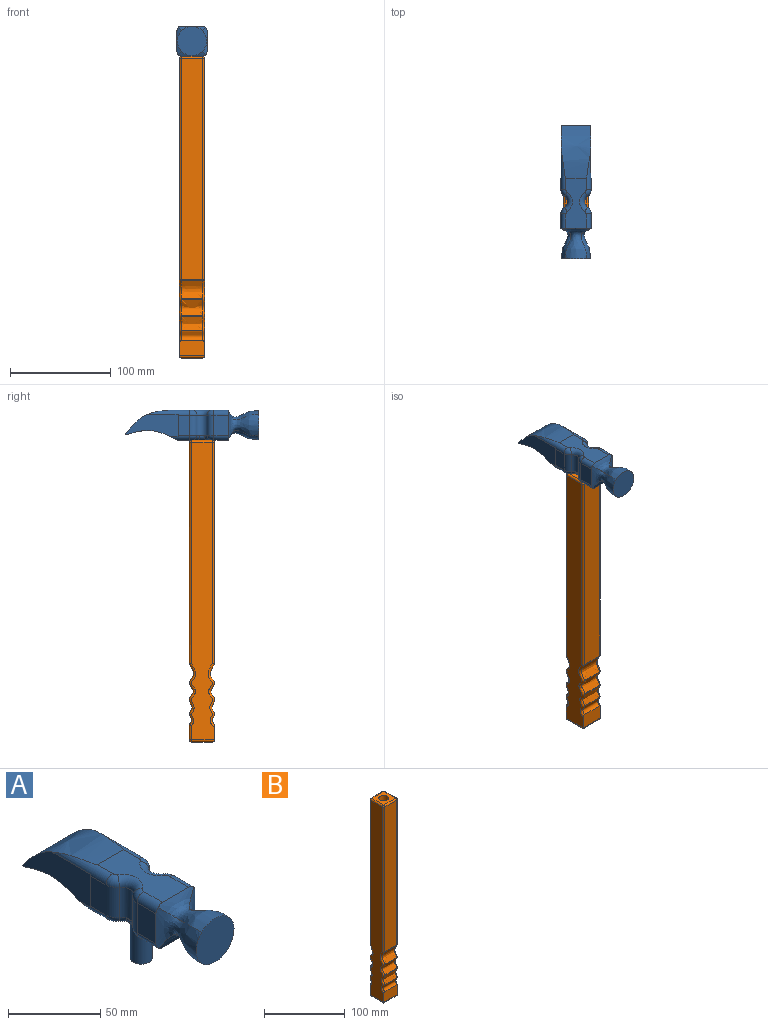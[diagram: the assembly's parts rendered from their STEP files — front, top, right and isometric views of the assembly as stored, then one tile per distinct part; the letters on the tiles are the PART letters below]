
ASSEMBLY  parts=2 mates=1
PART A: 51 faces, bbox 30x133.1x55 mm
  f0: plane 22.18x20mm, normal (0,0,-1), area 388.1mm2, adj f9,f25,f36,f37,f38,f43,f44,f45
  f1: plane 50x20mm, normal (0,0,1), area 812.3mm2, adj f11,f16,f27,f28,f29,f30,f31,f46
  f2: plane 20x11.8mm, normal (1,0,0), area 235.9mm2, adj f6,f21,f27,f32
  f3: plane 20x19.63mm, normal (0,0,-1), area 337.1mm2, adj f14,f25,f32,f33,f34,f39,f40,f41
  f4: plane 20x14.35mm, normal (-1,0,0), area 286.9mm2, adj f8,f23,f45,f50
  f5: plane 20x11.8mm, normal (-1,0,0), area 235.9mm2, adj f13,f24,f39,f46
  f6: plane 21.99x0.1mm, normal (0,1,0), area 2.1mm2, adj f2,f17,f27,f32
  f7: plane 29.01x29.01mm, normal (0,-1,0), area 660.9mm2, adj f8,f9,f10,f11
  f8: bspline ~30.4x30mm, area 683.9mm2, adj f4,f7,f9,f11,f45,f50
  f9: bspline ~30.4x30mm, area 683.9mm2, adj f0,f7,f8,f10,f38,f45
  f10: bspline ~30.4x30mm, area 683.9mm2, adj f7,f9,f11,f12,f31,f38
  f11: bspline ~30.4x30mm, area 683.9mm2, adj f1,f7,f8,f10,f31,f50
  f12: plane 20x14.35mm, normal (1,0,0), area 286.9mm2, adj f10,f22,f31,f38
  f13: plane 21.99x0.1mm, normal (0,1,0), area 2.1mm2, adj f5,f18,f39,f46
  f14: extruded ~51.69x29.8mm, area 1587.3mm2, adj f3,f15,f17,f18,f32,f39
  f15: plane 29.8x1.02mm, normal (0,0.32,-0.95), area 31.9mm2, adj f14,f16,f17,f18
  f16: extruded ~52.71x29.8mm, area 1671.4mm2, adj f1,f15,f17,f18,f27,f46
  f17: plane 52.71x22.75mm, normal (1,0,0), area 797.5mm2, adj f6,f14,f15,f16,f27,f32
  f18: plane 52.71x22.75mm, normal (-1,0,0), area 797.5mm2, adj f13,f14,f15,f16,f39,f46
  f19: cylinder r=6.36mm len=20mm, axis (0,0,1), area 249.4mm2, adj f23,f24,f41,f42,f43,f48
  f20: cylinder r=6.36mm len=20mm, axis (0,0,1), area 249.4mm2, adj f21,f22,f29,f34,f35,f36
  f21: cylinder r=8mm len=20mm, axis (0,0,1), area 156.8mm2, adj f2,f20,f28,f33
  f22: cylinder r=8mm len=20mm, axis (0,0,1), area 156.8mm2, adj f12,f20,f30,f37
  f23: cylinder r=8mm len=20mm, axis (0,0,1), area 156.8mm2, adj f4,f19,f44,f49
  f24: cylinder r=8mm len=20mm, axis (0,0,1), area 156.8mm2, adj f5,f19,f40,f47
  f25: cylinder r=6.01mm len=25mm, axis (0,0,1), area 944.8mm2, adj f0,f3,f26,f35,f42
  f26: plane 12.03x12.03mm, normal (0,0,-1), area 113.6mm2, adj f25
  f27: cylinder r=5mm len=41.57mm, axis (0,-1,0), area 204.3mm2, adj f1,f2,f6,f16,f17,f28
  f28: torus R=3mm, axis (0,0,1), area 47.6mm2, adj f1,f21,f27,f29
  f29: torus R=11.36mm, axis (0,0,1), area 125.9mm2, adj f1,f20,f28,f30
  f30: torus R=3mm, axis (0,0,1), area 47.6mm2, adj f1,f22,f29,f31
  f31: cylinder r=5mm len=14.92mm, axis (0,-1,0), area 114.9mm2, adj f1,f10,f11,f12,f30
  f32: cylinder r=5mm len=20.37mm, axis (0,-1,0), area 113.3mm2, adj f2,f3,f6,f14,f17,f33
  f33: torus R=3mm, axis (0,0,-1), area 47.6mm2, adj f3,f21,f32,f34
  f34: torus R=11.36mm, axis (0,0,-1), area 39.3mm2, adj f3,f20,f33,f35
  f35: bspline ~8.2x5mm, area 34.4mm2, adj f20,f25,f34,f36
  f36: torus R=11.36mm, axis (0,0,-1), area 39.3mm2, adj f0,f20,f35,f37
  f37: torus R=3mm, axis (0,0,-1), area 47.6mm2, adj f0,f22,f36,f38
  f38: cylinder r=5mm len=14.92mm, axis (0,-1,0), area 114.9mm2, adj f0,f9,f10,f12,f37
  f39: cylinder r=5mm len=20.37mm, axis (0,-1,0), area 113.3mm2, adj f3,f5,f13,f14,f18,f40
  f40: torus R=3mm, axis (0,0,-1), area 47.6mm2, adj f3,f24,f39,f41
  f41: torus R=11.36mm, axis (0,0,-1), area 39.3mm2, adj f3,f19,f40,f42
  f42: bspline ~8.2x5mm, area 34.4mm2, adj f19,f25,f41,f43
  f43: torus R=11.36mm, axis (0,0,-1), area 39.3mm2, adj f0,f19,f42,f44
  f44: torus R=3mm, axis (0,0,-1), area 47.6mm2, adj f0,f23,f43,f45
  f45: cylinder r=5mm len=14.92mm, axis (0,-1,0), area 114.9mm2, adj f0,f4,f8,f9,f44
  f46: cylinder r=5mm len=41.57mm, axis (0,-1,0), area 204.3mm2, adj f1,f5,f13,f16,f18,f47
  f47: torus R=3mm, axis (0,0,1), area 47.6mm2, adj f1,f24,f46,f48
  f48: torus R=11.36mm, axis (0,0,1), area 125.9mm2, adj f1,f19,f47,f49
  f49: torus R=3mm, axis (0,0,1), area 47.6mm2, adj f1,f23,f48,f50
  f50: cylinder r=5mm len=14.92mm, axis (0,-1,0), area 114.9mm2, adj f1,f4,f8,f11,f49
PART B: 51 faces, bbox 25.2x30.6x300.2 mm
  f0: plane 23.32x0.47mm, normal (0,1,0), area 6mm2, adj f9,f16,f23,f42
  f1: plane 23.33x0.91mm, normal (0,1,0), area 21.2mm2, adj f9,f22,f23,f42
  f2: plane 23x0.2mm, normal (0,1,0), area 4.5mm2, adj f9,f21,f22,f45
  f3: plane 220.5x21mm, normal (0,1,0), area 4630.6mm2, adj f16,f30,f36,f39
  f4: plane 296x22.89mm, normal (-1,0,0), area 5923mm2, adj f11,f29,f33,f37,f39,f42,f45,f46
  f5: plane 21.33x0.36mm, normal (0,-1,0), area 4.1mm2, adj f19,f20,f24,f29
  f6: plane 21.65x0.91mm, normal (0,-1,0), area 19.6mm2, adj f18,f19,f24,f29
  f7: plane 21.42x0.47mm, normal (0,-1,0), area 5.5mm2, adj f17,f18,f24,f29
  f8: plane 219.94x21mm, normal (0,-1,0), area 4618.7mm2, adj f25,f28,f32,f33
  f9: plane 296x25.18mm, normal (1,0,0), area 6096.6mm2, adj f0,f1,f2,f11,f16,f21,f22,f23
  f10: plane 21x15.32mm, normal (0,1,0), area 321.7mm2, adj f21,f41,f47,f50
  f11: plane 25x15.32mm, normal (0,-1,0), area 380.4mm2, adj f4,f9,f20,f24,f29,f43
  f12: plane 21x20.85mm, normal (0,0,1), area 324.3mm2, adj f14,f31,f32,f36,f37
  f13: plane 21x20.85mm, normal (0,0,-1), area 437.9mm2, adj f40,f43,f46,f47
  f14: cylinder r=6.02mm len=24.8mm, axis (0,0,1), area 937.3mm2, adj f12,f15
  f15: plane 12.03x12.03mm, normal (0,0,1), area 113.7mm2, adj f14
  f16: extruded ~23x18.71mm, area 475.5mm2, adj f0,f3,f9,f30,f42
  f17: extruded ~21x18.23mm, area 425.8mm2, adj f7,f24,f28,f29
  f18: extruded ~21x15.96mm, area 377.8mm2, adj f6,f7,f24,f29
  f19: extruded ~21x13.87mm, area 313.7mm2, adj f5,f6,f24,f29
  f20: extruded ~21x10.27mm, area 241.1mm2, adj f5,f11,f24,f29
  f21: extruded ~23x10.27mm, area 260.6mm2, adj f2,f9,f10,f41,f48
  f22: extruded ~23x13.87mm, area 343.5mm2, adj f1,f2,f9,f42
  f23: extruded ~23x15.96mm, area 413.8mm2, adj f0,f1,f9,f42
  f24: bspline ~67.01x9.35mm, area 213.1mm2, adj f5,f6,f7,f9,f11,f17,f18,f19
  f25: cylinder r=2mm len=219.94mm, axis (0,0,1), area 691mm2, adj f8,f9,f26,f27
  f26: sphere r=2mm, area 1.7mm2, adj f24,f25,f28
  f27: sphere r=2mm, area 6.3mm2, adj f25,f31,f32
  f28: cylinder r=2mm len=21.55mm, axis (-1,0,0), area 23.5mm2, adj f8,f17,f26,f29,f33
  f29: bspline ~69.59x11.3mm, area 215mm2, adj f4,f5,f6,f7,f11,f17,f18,f19
  f30: cylinder r=2mm len=223.85mm, axis (0,0,-1), area 698mm2, adj f3,f9,f16,f34
  f31: cylinder r=2mm len=20.85mm, axis (0,-1,0), area 65.5mm2, adj f9,f12,f27,f34
  f32: cylinder r=2mm len=21mm, axis (-1,0,0), area 66mm2, adj f8,f12,f27,f35
  f33: cylinder r=2mm len=220.48mm, axis (0,0,-1), area 691.8mm2, adj f4,f8,f28,f29,f35
  f34: sphere r=2mm, area 4mm2, adj f30,f31,f36
  f35: sphere r=2mm, area 6.3mm2, adj f32,f33,f37
  f36: cylinder r=2mm len=21mm, axis (1,0,0), area 66mm2, adj f3,f12,f34,f38
  f37: cylinder r=2mm len=20.85mm, axis (0,1,0), area 65.5mm2, adj f4,f12,f35,f38
  f38: sphere r=2mm, area 8.6mm2, adj f36,f37,f39
  f39: cylinder r=2mm len=220.5mm, axis (0,0,1), area 691.8mm2, adj f3,f4,f38,f42
  f40: cylinder r=2mm len=22.85mm, axis (0,1,0), area 68.7mm2, adj f9,f13,f43,f44
  f41: cylinder r=2mm len=18.07mm, axis (0,0,-1), area 52.5mm2, adj f9,f10,f21,f44
  f42: bspline ~51.24x6.46mm, area 173.3mm2, adj f0,f1,f4,f16,f22,f23,f39,f45
  f43: cylinder r=2mm len=25mm, axis (1,0,0), area 72.3mm2, adj f11,f13,f40,f46
  f44: sphere r=2mm, area 4mm2, adj f40,f41,f47
  f45: cylinder r=2mm len=2mm, axis (0,0,1), area 0.5mm2, adj f2,f4,f42,f48
  f46: cylinder r=2mm len=22.85mm, axis (0,-1,0), area 68.7mm2, adj f4,f13,f43,f49
  f47: cylinder r=2mm len=21mm, axis (-1,0,0), area 66mm2, adj f10,f13,f44,f49
  f48: bspline ~12.44x4.82mm, area 36.5mm2, adj f4,f21,f45,f50
  f49: sphere r=2mm, area 8.6mm2, adj f46,f47,f50
  f50: cylinder r=2mm len=15.32mm, axis (0,0,1), area 47mm2, adj f4,f10,f48,f49
PLACE A t=(12.96,-45.76,172.41)mm
PLACE B t=(46.23,41.21,-142.79)mm
MATE fastened B.f14 <-> A.f25  axis (0,0,1) through (12.96,10.91,132.41)mm
